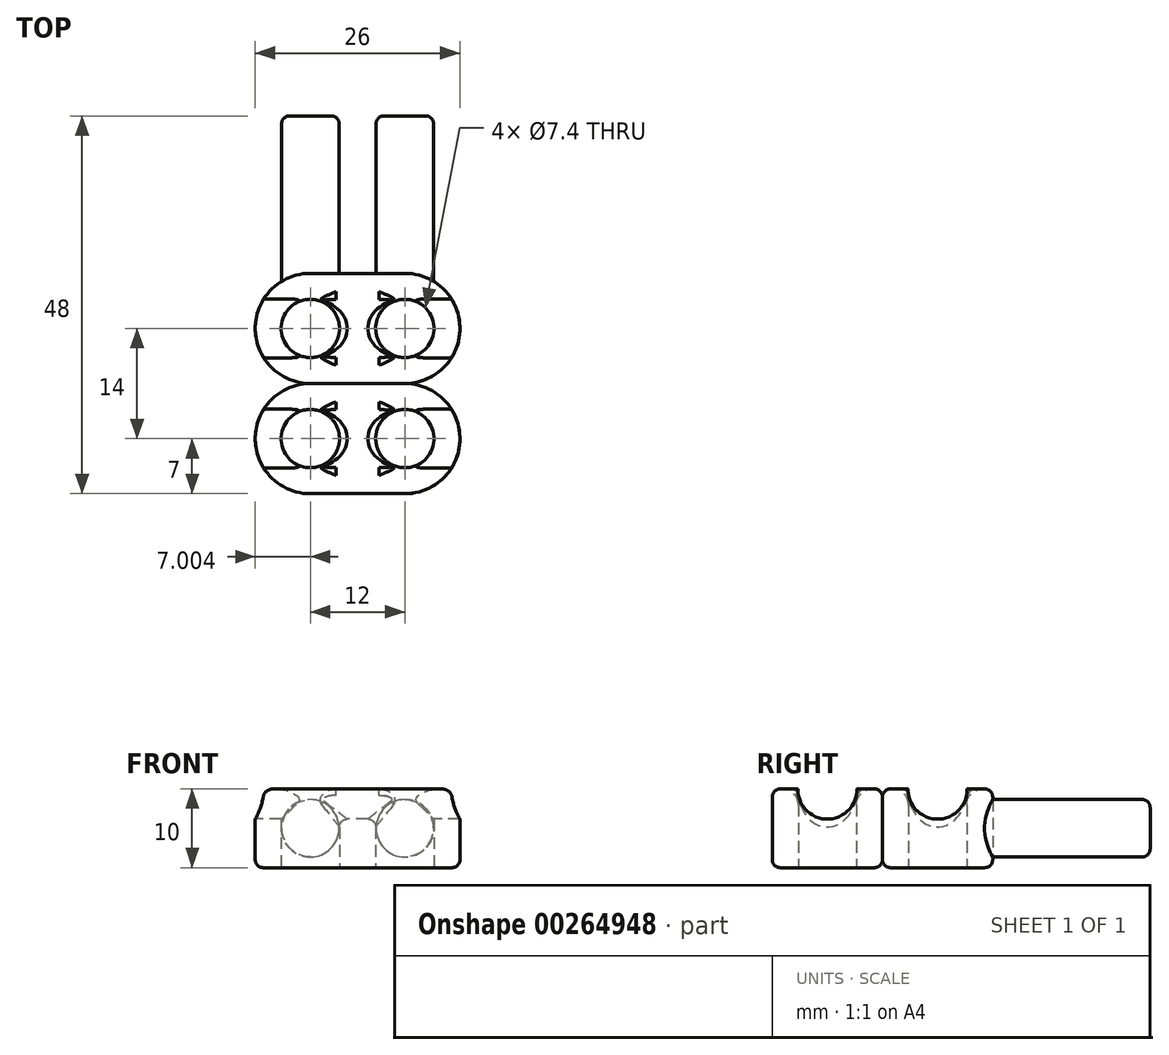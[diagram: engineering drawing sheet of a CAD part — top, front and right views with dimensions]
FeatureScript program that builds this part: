
annotation { "Feature Type Name" : "Feature", "Feature Type Description" : "" }
export const myFeature = defineFeature(function(context is Context, id is Id, definition is map)
    precondition{}
    {
        {
            var Q0;
            Q0=qCreatedBy(makeId("Top.planeOp"),FACE);
            var sketch = newSketch(context, id + "F0", { "sketchPlane" : qUnion([Q0])});
            skArc(sketch, "E0", {"start": v(-7.14, 7) * mm, "mid": v(-14.14, 0) * mm, "end": v(-7.14, -7) * mm});
            skArc(sketch, "E1", {"start": v(4.86, -7) * mm, "mid": v(11.86, 0) * mm, "end": v(4.86, 7) * mm});
            skLineSegment(sketch, "E2", {"start": v(-7.14, 7) * mm, "end": v(4.86, 7) * mm});
            skLineSegment(sketch, "E3", {"start": v(-7.14, -7) * mm, "end": v(4.86, -7) * mm});
            skCircle(sketch, "E4", {"center": v(-7.14, 0) * mm, "radius": 3.7 * mm});
            skCircle(sketch, "E5", {"center": v(4.86, 0) * mm, "radius": 3.7 * mm});
            skSolve(sketch);
        }
        {
            var Q0;
            Q0=makeQuery(id+"F0.imprint","IMPRINT",FACE,{"disambiguationData":[TD([[makeQuery(id+"F0.imprint","IMPRINT",EDGE,{"derivedFrom":sQuery(id+"F0.wireOp",EDGE,"E0")}),1.0]])]});
            extrude(context, id + "F1", {"entities" : qUnion([Q0]), "depth" : 10 * mm});
        }
        {
            var Q0;
            Q0=makeQuery(id+"F1.opExtrude","CAP_EDGE",EDGE,{"disambiguationData":[OSD([sQuery(id+"F0.wireOp",EDGE,"E4")])],"isStart":false});
            var Q1;
            Q1=makeQuery(id+"F1.opExtrude","CAP_EDGE",EDGE,{"disambiguationData":[OSD([sQuery(id+"F0.wireOp",EDGE,"E5")])],"isStart":false});
            fillet(context, id + "F2", {"entities" : qUnion([Q0, Q1]), "radius" : 2 * mm, "tangentPropagation" : true, "allowEdgeOverflow" : false});
        }
        {
            var Q0;
            Q0=makeQuery(id+"F1.opExtrude","CAP_EDGE",EDGE,{"disambiguationData":[OSD([sQuery(id+"F0.wireOp",EDGE,"E0")])],"isStart":false});
            var Q1;
            Q1=makeQuery(id+"F1.opExtrude","CAP_EDGE",EDGE,{"disambiguationData":[OSD([sQuery(id+"F0.wireOp",EDGE,"E1")])],"isStart":true});
            fillet(context, id + "F3", {"entities" : qUnion([Q0, Q1]), "radius" : 1 * mm, "tangentPropagation" : true, "allowEdgeOverflow" : false});
        }
        {
            var Q0;
            Q0=qCreatedBy(makeId("Right.planeOp"),FACE);
            var sketch = newSketch(context, id + "F4", { "sketchPlane" : qUnion([Q0])});
            skCircle(sketch, "E6", {"center": v(0, 9.91) * mm, "radius": 3.75 * mm});
            skSolve(sketch);
        }
        {
            var Q0;
            Q0=makeQuery(id+"F4.imprint","IMPRINT",FACE,{"disambiguationData":[TD([[makeQuery(id+"F4.imprint","IMPRINT",EDGE,{"derivedFrom":sQuery(id+"F4.wireOp",EDGE,"E6")}),1.0]])]});
            var Q1;
            Q1=sQuery(id+"F4.wireOp",EDGE,"E6");
            extrude(context, id + "F5", {"entities" : qUnion([Q0]), "operationType" : NewBodyOperationType.REMOVE, "surfaceEntities" : qUnion([Q1]), "endBound" : BoundingType.SYMMETRIC, "depth" : 30 * mm});
        }
        {
            var Q0;
            Q0=makeQuery(id+"F5.boolean.opBoolean","INTERSECT",EDGE,{"disambiguationData":[OD(1.0)],"derivedFrom":[makeQuery(id+"F1.opExtrude","SWEPT_FACE",FACE,{"disambiguationData":[OSD([sQuery(id+"F0.wireOp",EDGE,"E4")])]}),makeQuery(id+"F5.opExtrude","SWEPT_FACE",FACE,{"disambiguationData":[OSD([sQuery(id+"F4.wireOp",EDGE,"E6")])]})]});
            var Q1;
            Q1=makeQuery(id+"F5.boolean.opBoolean","INTERSECT",EDGE,{"disambiguationData":[OD(1.0)],"derivedFrom":[makeQuery(id+"F1.opExtrude","SWEPT_FACE",FACE,{"disambiguationData":[OSD([sQuery(id+"F0.wireOp",EDGE,"E5")])]}),makeQuery(id+"F5.opExtrude","SWEPT_FACE",FACE,{"disambiguationData":[OSD([sQuery(id+"F4.wireOp",EDGE,"E6")])]})]});
            fillet(context, id + "F6", {"entities" : qUnion([Q0, Q1]), "radius" : 1 * mm, "tangentPropagation" : true, "allowEdgeOverflow" : false});
        }
        {
            var Q0;
            Q0=makeQuery(id+"F1.opExtrude","SWEPT_BODY",BODY,{"disambiguationData":[OSD([sQuery(id+"F0.wireOp",EDGE,"E0"),sQuery(id+"F0.wireOp",EDGE,"E1"),sQuery(id+"F0.wireOp",EDGE,"E2"),sQuery(id+"F0.wireOp",EDGE,"E3"),sQuery(id+"F0.wireOp",EDGE,"E4"),sQuery(id+"F0.wireOp",EDGE,"E5")])]});
            transform(context, id + "F7", {"entities" : qUnion([Q0]), "transformType" : TransformType.TRANSLATION_3D, "dx" : 0 * mm, "dy" : 14 * mm, "dz" : 0 * mm, "makeCopy" : true});
        }
        {
            var Q0;
            Q0=makeQuery(id+"F7.opPattern","COPY",FACE,{"derivedFrom":makeQuery(id+"F1.opExtrude","SWEPT_FACE",FACE,{"disambiguationData":[OSD([sQuery(id+"F0.wireOp",EDGE,"E2")])]}),"instanceName":"1"});
            var sketch = newSketch(context, id + "F8", { "sketchPlane" : qUnion([Q0])});
            skCircle(sketch, "E7", {"center": v(-4.86, 5) * mm, "radius": 3.65 * mm});
            skCircle(sketch, "E8", {"center": v(7.14, 5) * mm, "radius": 3.65 * mm});
            skSolve(sketch);
        }
        {
            var Q0;
            {var subQ0=sQuery(id+"F8.wireOp",EDGE,"E7");var subQ1=makeQuery(id+"F7.opPattern","COPY",EDGE,{"derivedFrom":makeQuery(id+"F1.opExtrude","SWEPT_EDGE",EDGE,{"disambiguationData":[OSD([sQuery(id+"F0.wireOp",EDGE,"E1"),sQuery(id+"F0.wireOp",EDGE,"E2")])]}),"instanceName":"1"});var subQ2=makeQuery(id+"F8.imprint","INTERSECT",VERTEX,{"disambiguationData":[OD(0.0)],"derivedFrom":[subQ1,subQ0]});Q0=makeQuery(id+"F8.imprint","IMPRINT",FACE,{"disambiguationData":[TD([[makeQuery(id+"F8.imprint","IMPRINT",EDGE,{"disambiguationData":[TD([[subQ2,1.0]])],"derivedFrom":subQ0}),1.0]])]});}
            var Q1;
            {var subQ0=sQuery(id+"F8.wireOp",EDGE,"E7");var subQ1=makeQuery(id+"F7.opPattern","COPY",EDGE,{"derivedFrom":makeQuery(id+"F1.opExtrude","SWEPT_EDGE",EDGE,{"disambiguationData":[OSD([sQuery(id+"F0.wireOp",EDGE,"E1"),sQuery(id+"F0.wireOp",EDGE,"E2")])]}),"instanceName":"1"});var subQ2=makeQuery(id+"F8.imprint","INTERSECT",VERTEX,{"disambiguationData":[OD(0.0)],"derivedFrom":[subQ1,subQ0]});Q1=makeQuery(id+"F8.imprint","IMPRINT",FACE,{"disambiguationData":[TD([[makeQuery(id+"F8.imprint","IMPRINT",EDGE,{"disambiguationData":[TD([[subQ2,-1.0]])],"derivedFrom":subQ0}),1.0]])]});}
            var Q2;
            {var subQ0=sQuery(id+"F8.wireOp",EDGE,"E8");var subQ1=makeQuery(id+"F7.opPattern","COPY",EDGE,{"derivedFrom":makeQuery(id+"F1.opExtrude","SWEPT_EDGE",EDGE,{"disambiguationData":[OSD([sQuery(id+"F0.wireOp",EDGE,"E0"),sQuery(id+"F0.wireOp",EDGE,"E2")])]}),"instanceName":"1"});var subQ2=makeQuery(id+"F8.imprint","INTERSECT",VERTEX,{"disambiguationData":[OD(0.0)],"derivedFrom":[subQ1,subQ0]});Q2=makeQuery(id+"F8.imprint","IMPRINT",FACE,{"disambiguationData":[TD([[makeQuery(id+"F8.imprint","IMPRINT",EDGE,{"disambiguationData":[TD([[subQ2,1.0]])],"derivedFrom":subQ0}),1.0]])]});}
            var Q3;
            {var subQ0=sQuery(id+"F8.wireOp",EDGE,"E8");var subQ1=makeQuery(id+"F7.opPattern","COPY",EDGE,{"derivedFrom":makeQuery(id+"F1.opExtrude","SWEPT_EDGE",EDGE,{"disambiguationData":[OSD([sQuery(id+"F0.wireOp",EDGE,"E0"),sQuery(id+"F0.wireOp",EDGE,"E2")])]}),"instanceName":"1"});var subQ2=makeQuery(id+"F8.imprint","INTERSECT",VERTEX,{"disambiguationData":[OD(0.0)],"derivedFrom":[subQ1,subQ0]});Q3=makeQuery(id+"F8.imprint","IMPRINT",FACE,{"disambiguationData":[TD([[makeQuery(id+"F8.imprint","IMPRINT",EDGE,{"disambiguationData":[TD([[subQ2,-1.0]])],"derivedFrom":subQ0}),1.0]])]});}
            extrude(context, id + "F9", {"entities" : qUnion([Q0, Q1, Q2, Q3]), "operationType" : NewBodyOperationType.ADD, "depth" : 20 * mm, "hasSecondDirection" : true, "secondDirectionOppositeDirection" : true, "secondDirectionDepth" : 3 * mm});
        }
        {
            var Q0;
            Q0=makeQuery(id+"F9.opExtrude","CAP_EDGE",EDGE,{"disambiguationData":[OSD([sQuery(id+"F8.wireOp",EDGE,"E8")])],"isStart":false});
            var Q1;
            Q1=makeQuery(id+"F9.opExtrude","CAP_EDGE",EDGE,{"disambiguationData":[OSD([sQuery(id+"F8.wireOp",EDGE,"E7")])],"isStart":false});
            fillet(context, id + "F10", {"entities" : qUnion([Q0, Q1]), "radius" : 1 * mm, "tangentPropagation" : true, "allowEdgeOverflow" : false});
        }
    });
